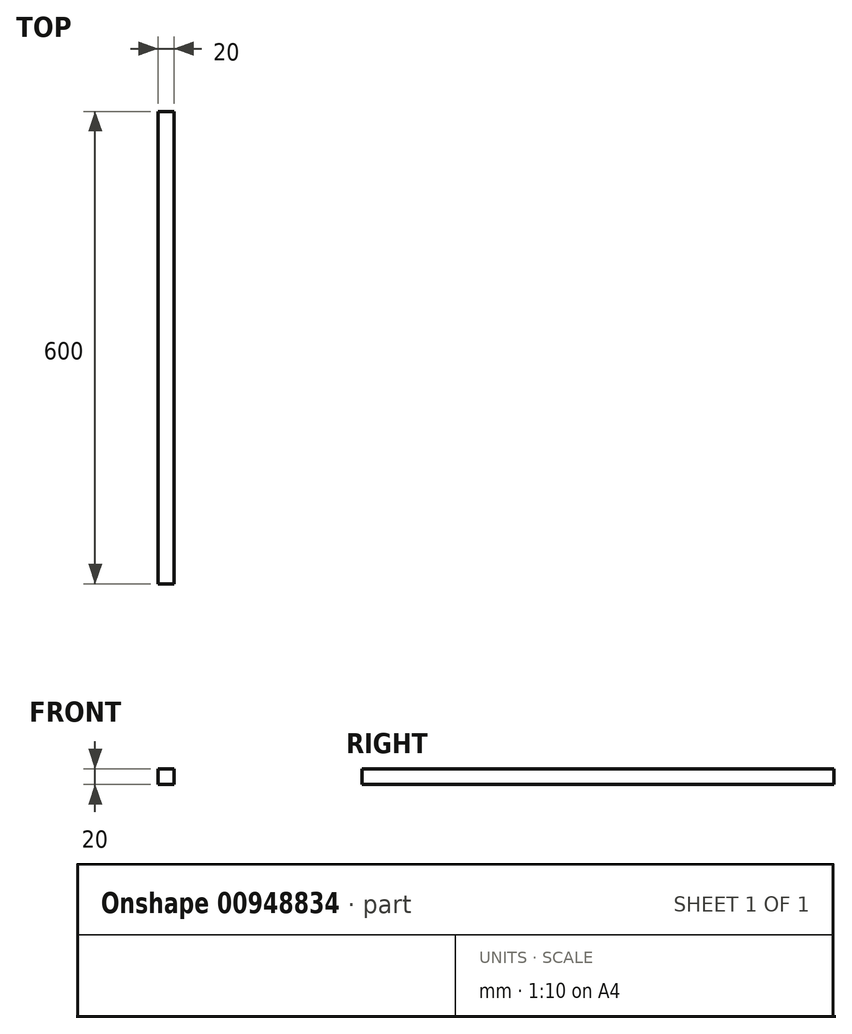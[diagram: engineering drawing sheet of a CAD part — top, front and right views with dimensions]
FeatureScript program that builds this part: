
annotation { "Feature Type Name" : "Feature", "Feature Type Description" : "" }
export const myFeature = defineFeature(function(context is Context, id is Id, definition is map)
    precondition{}
    {
        {
            var Q0;
            Q0=qCreatedBy(makeId("Front.planeOp"),FACE);
            var sketch = newSketch(context, id + "F0", { "sketchPlane" : qUnion([Q0])});
            skLineSegment(sketch, "E0.bottom", {"start": v(10, -10) * mm, "end": v(-10, -10) * mm});
            skLineSegment(sketch, "E0.top", {"start": v(10, 10) * mm, "end": v(-10, 10) * mm});
            skLineSegment(sketch, "E0.left", {"start": v(10, -10) * mm, "end": v(10, 10) * mm});
            skLineSegment(sketch, "E0.right", {"start": v(-10, -10) * mm, "end": v(-10, 10) * mm});
            skPoint(sketch, "E0.middle", {"position": v(0, 0) * mm});
            skSolve(sketch);
        }
        {
            var Q0;
            Q0=qSketchRegion(id+"F0",true);
            extrude(context, id + "F1", {"entities" : qUnion([Q0]), "depth" : 600 * mm, "offsetDistance" : 25 * mm});
        }
    });
